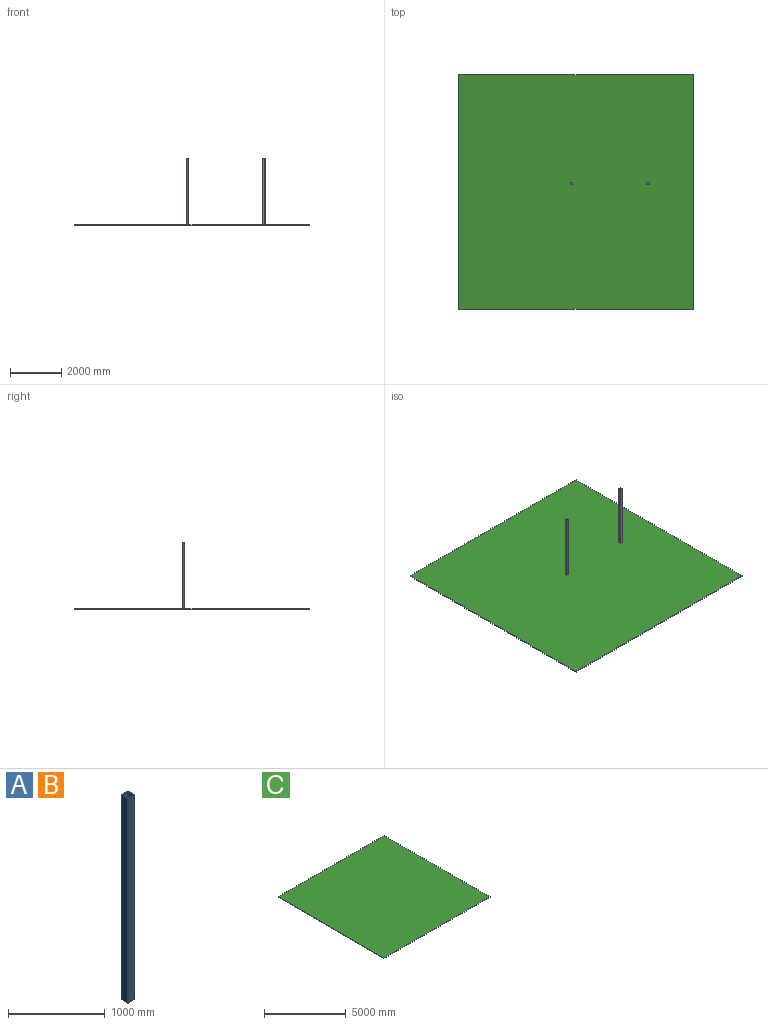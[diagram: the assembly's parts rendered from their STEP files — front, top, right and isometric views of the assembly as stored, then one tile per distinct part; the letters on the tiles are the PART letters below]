
ASSEMBLY  parts=3 mates=3
PART A: 18 faces, bbox 101.6x101.6x2590.8 mm
  f0: cylinder r=3.17mm len=2590.8mm, axis (0,0,-1), area 12921mm2, adj f1,f15,f16,f17
  f1: plane 2590.8x95.25mm, normal (0,-1,0), area 246773.7mm2, adj f0,f2,f16,f17
  f2: cylinder r=3.17mm len=2590.8mm, axis (0,0,-1), area 12921mm2, adj f1,f3,f16,f17
  f3: plane 2590.8x95.25mm, normal (1,0,0), area 246773.7mm2, adj f2,f4,f16,f17
  f4: cylinder r=3.17mm len=2590.8mm, axis (0,0,-1), area 12921mm2, adj f3,f5,f16,f17
  f5: plane 2590.8x95.25mm, normal (0,1,0), area 246773.7mm2, adj f4,f6,f16,f17
  f6: cylinder r=3.17mm len=2590.8mm, axis (0,0,-1), area 12921mm2, adj f5,f15,f16,f17
  f7: plane 2590.8x76.2mm, normal (0,1,0), area 197419mm2, adj f8,f14,f16,f17
  f8: cylinder r=3.17mm len=2590.8mm, axis (0,0,-1), area 12921mm2, adj f7,f9,f16,f17
  f9: plane 2590.8x76.2mm, normal (1,0,0), area 197419mm2, adj f8,f10,f16,f17
  f10: cylinder r=3.17mm len=2590.8mm, axis (0,0,-1), area 12921mm2, adj f9,f11,f16,f17
  f11: plane 2590.8x76.2mm, normal (0,-1,0), area 197419mm2, adj f10,f12,f16,f17
  f12: cylinder r=3.17mm len=2590.8mm, axis (0,0,-1), area 12921mm2, adj f11,f13,f16,f17
  f13: plane 2590.8x76.2mm, normal (-1,0,0), area 197419mm2, adj f12,f14,f16,f17
  f14: cylinder r=3.17mm len=2590.8mm, axis (0,0,-1), area 12921mm2, adj f7,f13,f16,f17
  f15: plane 2590.8x95.25mm, normal (-1,0,0), area 246773.7mm2, adj f0,f6,f16,f17
  f16: plane 101.6x101.6mm, normal (0,0,1), area 3508.1mm2, adj f0,f1,f2,f3,f4,f5,f6,f7
  f17: plane 101.6x101.6mm, normal (0,0,-1), area 3508.1mm2, adj f0,f1,f2,f3,f4,f5,f6,f7
PART B: same geometry as A
PART C: 6 faces, bbox 9144x9144x25.4 mm
  f0: plane 9144x25.4mm, normal (1,0,0), area 232257.6mm2, adj f1,f3,f4,f5
  f1: plane 9144x25.4mm, normal (0,1,0), area 232257.6mm2, adj f0,f2,f4,f5
  f2: plane 9144x25.4mm, normal (-1,0,0), area 232257.6mm2, adj f1,f3,f4,f5
  f3: plane 9144x25.4mm, normal (0,-1,0), area 232257.6mm2, adj f0,f2,f4,f5
  f4: plane 9144x9144mm, normal (0,0,1), area 83612736mm2, adj f0,f1,f2,f3
  f5: plane 9144x9144mm, normal (0,0,-1), area 83612736mm2, adj f0,f1,f2,f3
PLACE A rot(axis=(0,0,-1),0deg) t=(-1852.06,735.77,0)mm
PLACE B rot(axis=(0,0,-1),0deg) t=(1115.85,735.77,0)mm
PLACE C t=(-1683.78,401.81,-25.4)mm
MATE planar B.f5 <-> A.f5  axis (0,1,0) through (1115.85,786.57,1295.4)mm
MATE planar C.f4 <-> A.f17  axis (0,0,1) through (-1683.78,401.81,0)mm
MATE planar C.f4 <-> B.f17  axis (0,0,1) through (-1683.78,401.81,0)mm
